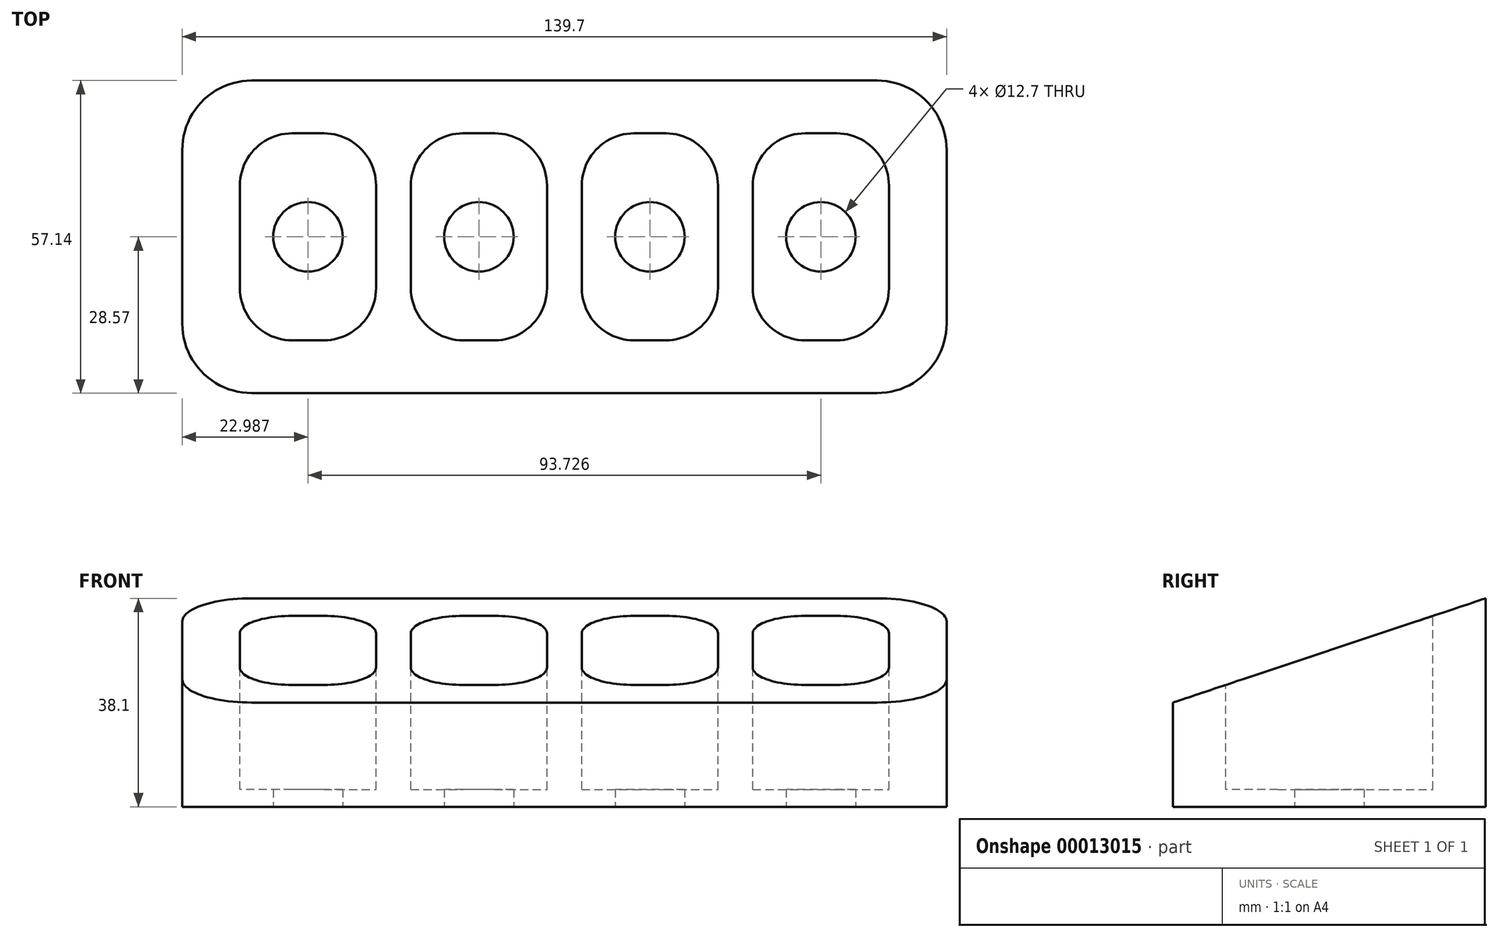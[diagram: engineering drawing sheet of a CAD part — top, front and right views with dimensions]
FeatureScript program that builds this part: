
annotation { "Feature Type Name" : "Feature", "Feature Type Description" : "" }
export const myFeature = defineFeature(function(context is Context, id is Id, definition is map)
    precondition{}
    {
        {
            var Q0;
            Q0=qCreatedBy(makeId("Top.planeOp"),FACE);
            var sketch = newSketch(context, id + "F0", { "sketchPlane" : qUnion([Q0])});
            skLineSegment(sketch, "E0.rect.bottom", {"start": v(69.85, 28.58) * mm, "end": v(-69.85, 28.58) * mm});
            skLineSegment(sketch, "E0.rect.top", {"start": v(69.85, -28.57) * mm, "end": v(-69.85, -28.57) * mm});
            skLineSegment(sketch, "E0.rect.left", {"start": v(69.85, 28.58) * mm, "end": v(69.85, -28.57) * mm});
            skLineSegment(sketch, "E0.rect.right", {"start": v(-69.85, 28.58) * mm, "end": v(-69.85, -28.57) * mm});
            skPoint(sketch, "E0.rect.middle", {"position": v(0, 0) * mm});
            skSolve(sketch);
        }
        {
            var Q0;
            Q0 = qSketchRegion(id + "F0", true);
            extrude(context, id + "F1", {"entities" : qUnion([Q0]), "depth" : 38.1 * mm});
        }
        {
            var Q0;
            Q0=makeQuery(id+"F1.opExtrude","CAP_FACE",FACE,{"disambiguationData":[OSD([sQuery(id+"F0.wireOp",EDGE,"E0.rect.bottom"),sQuery(id+"F0.wireOp",EDGE,"E0.rect.top"),sQuery(id+"F0.wireOp",EDGE,"E0.rect.left"),sQuery(id+"F0.wireOp",EDGE,"E0.rect.right")])],"isStart":false});
            var sketch = newSketch(context, id + "F2", { "sketchPlane" : qUnion([Q0])});
            skLineSegment(sketch, "E1.rect.bottom", {"start": v(-3.18, -18.92) * mm, "end": v(-28.07, -18.92) * mm});
            skLineSegment(sketch, "E1.rect.top", {"start": v(-3.17, 18.92) * mm, "end": v(-28.07, 18.92) * mm});
            skLineSegment(sketch, "E1.rect.left", {"start": v(-3.18, -18.92) * mm, "end": v(-3.17, 18.92) * mm});
            skLineSegment(sketch, "E1.rect.right", {"start": v(-28.07, -18.92) * mm, "end": v(-28.07, 18.92) * mm});
            skPoint(sketch, "E1.rect.middle", {"position": v(-15.62, 0) * mm});
            skLineSegment(sketch, "E2", {"start": v(0, -48.44) * mm, "end": v(0, 55.61) * mm, "construction": true});
            skLineSegment(sketch, "E3.1.0.0", {"start": v(-34.42, 18.92) * mm, "end": v(-59.3, 18.92) * mm});
            skLineSegment(sketch, "E3.1.0.1", {"start": v(-59.3, -18.92) * mm, "end": v(-59.3, 18.92) * mm});
            skLineSegment(sketch, "E3.1.0.2", {"start": v(-34.42, -18.92) * mm, "end": v(-34.42, 18.92) * mm});
            skLineSegment(sketch, "E3.1.0.3", {"start": v(-34.42, -18.92) * mm, "end": v(-59.3, -18.92) * mm});
            skLineSegment(sketch, "E3.direction1", {"start": v(-28.07, 18.92) * mm, "end": v(-59.3, 18.92) * mm});
            skLineSegment(sketch, "E4.0.MirrorCS", {"start": v(3.18, -18.92) * mm, "end": v(3.17, 18.92) * mm});
            skLineSegment(sketch, "E4.1.MirrorCS", {"start": v(3.17, 18.92) * mm, "end": v(28.07, 18.92) * mm});
            skLineSegment(sketch, "E4.2.MirrorCS", {"start": v(28.07, -18.92) * mm, "end": v(28.07, 18.92) * mm});
            skLineSegment(sketch, "E4.3.MirrorCS", {"start": v(3.18, -18.92) * mm, "end": v(28.07, -18.92) * mm});
            skLineSegment(sketch, "E4.4.MirrorCS", {"start": v(34.42, -18.92) * mm, "end": v(59.3, -18.92) * mm});
            skLineSegment(sketch, "E4.5.MirrorCS", {"start": v(59.3, -18.92) * mm, "end": v(59.3, 18.92) * mm});
            skLineSegment(sketch, "E4.6.MirrorCS", {"start": v(34.42, 18.92) * mm, "end": v(59.3, 18.92) * mm});
            skLineSegment(sketch, "E4.7.MirrorCS", {"start": v(34.42, -18.92) * mm, "end": v(34.42, 18.92) * mm});
            skSolve(sketch);
        }
        {
            var Q0;
            Q0 = qSketchRegion(id + "F2", true);
            extrude(context, id + "F3", {"entities" : qUnion([Q0]), "operationType" : NewBodyOperationType.REMOVE, "oppositeDirection" : true, "depth" : 34.92 * mm});
        }
        {
            var Q0;
            Q0=makeQuery(id+"F1.opExtrude","SWEPT_FACE",FACE,{"disambiguationData":[OSD([sQuery(id+"F0.wireOp",EDGE,"E0.rect.left")])]});
            var sketch = newSketch(context, id + "F4", { "sketchPlane" : qUnion([Q0])});
            skLineSegment(sketch, "E5", {"start": v(28.57, 38.1) * mm, "end": v(-28.58, 19.05) * mm});
            skLineSegment(sketch, "E6", {"start": v(-28.58, 19.05) * mm, "end": v(-28.58, 38.1) * mm});
            skLineSegment(sketch, "E7", {"start": v(-28.58, 38.1) * mm, "end": v(28.57, 38.1) * mm});
            skSolve(sketch);
        }
        {
            var Q0;
            Q0=makeQuery(id+"F4.imprint","IMPRINT",FACE,{"disambiguationData":[TD([[makeQuery(id+"F4.imprint","IMPRINT",EDGE,{"derivedFrom":sQuery(id+"F4.wireOp",EDGE,"E5")}),-1.0]])]});
            extrude(context, id + "F5", {"entities" : qUnion([Q0]), "operationType" : NewBodyOperationType.REMOVE, "endBound" : BoundingType.THROUGH_ALL, "oppositeDirection" : true, "depth" : 25.4 * mm});
        }
        {
            var Q0;
            Q0=makeQuery(id+"F1.opExtrude","SWEPT_EDGE",EDGE,{"disambiguationData":[OSD([sQuery(id+"F0.wireOp",EDGE,"E0.rect.top"),sQuery(id+"F0.wireOp",EDGE,"E0.rect.left")])]});
            var Q1;
            Q1=makeQuery(id+"F1.opExtrude","SWEPT_EDGE",EDGE,{"disambiguationData":[OSD([sQuery(id+"F0.wireOp",EDGE,"E0.rect.bottom"),sQuery(id+"F0.wireOp",EDGE,"E0.rect.left")])]});
            var Q2;
            Q2=makeQuery(id+"F1.opExtrude","SWEPT_EDGE",EDGE,{"disambiguationData":[OSD([sQuery(id+"F0.wireOp",EDGE,"E0.rect.top"),sQuery(id+"F0.wireOp",EDGE,"E0.rect.right")])]});
            var Q3;
            Q3=makeQuery(id+"F1.opExtrude","SWEPT_EDGE",EDGE,{"disambiguationData":[OSD([sQuery(id+"F0.wireOp",EDGE,"E0.rect.bottom"),sQuery(id+"F0.wireOp",EDGE,"E0.rect.right")])]});
            fillet(context, id + "F6", {"entities" : qUnion([Q0, Q1, Q2, Q3]), "radius" : 12.7 * mm, "tangentPropagation" : true, "allowEdgeOverflow" : false});
        }
        {
            var Q0;
            Q0=makeQuery(id+"F3.boolean.opBoolean","COPY",EDGE,{"derivedFrom":makeQuery(id+"F3.opExtrude","SWEPT_EDGE",EDGE,{"disambiguationData":[OSD([sQuery(id+"F2.wireOp",EDGE,"E3.1.0.1"),sQuery(id+"F2.wireOp",EDGE,"E3.direction1")])]})});
            var Q1;
            Q1=makeQuery(id+"F3.boolean.opBoolean","COPY",EDGE,{"derivedFrom":makeQuery(id+"F3.opExtrude","SWEPT_EDGE",EDGE,{"disambiguationData":[OSD([sQuery(id+"F2.wireOp",EDGE,"E3.1.0.2"),sQuery(id+"F2.wireOp",EDGE,"E3.direction1")])]})});
            var Q2;
            Q2=makeQuery(id+"F3.boolean.opBoolean","COPY",EDGE,{"derivedFrom":makeQuery(id+"F3.opExtrude","SWEPT_EDGE",EDGE,{"disambiguationData":[OSD([sQuery(id+"F2.wireOp",EDGE,"E1.rect.top"),sQuery(id+"F2.wireOp",EDGE,"E1.rect.right")])]})});
            var Q3;
            Q3=makeQuery(id+"F3.boolean.opBoolean","COPY",EDGE,{"derivedFrom":makeQuery(id+"F3.opExtrude","SWEPT_EDGE",EDGE,{"disambiguationData":[OSD([sQuery(id+"F2.wireOp",EDGE,"E1.rect.top"),sQuery(id+"F2.wireOp",EDGE,"E1.rect.left")])]})});
            var Q4;
            Q4=makeQuery(id+"F3.boolean.opBoolean","COPY",EDGE,{"derivedFrom":makeQuery(id+"F3.opExtrude","SWEPT_EDGE",EDGE,{"disambiguationData":[OSD([sQuery(id+"F2.wireOp",EDGE,"E4.1.MirrorCS"),sQuery(id+"F2.wireOp",EDGE,"E4.2.MirrorCS")])]})});
            var Q5;
            Q5=makeQuery(id+"F3.boolean.opBoolean","COPY",EDGE,{"derivedFrom":makeQuery(id+"F3.opExtrude","SWEPT_EDGE",EDGE,{"disambiguationData":[OSD([sQuery(id+"F2.wireOp",EDGE,"E4.5.MirrorCS"),sQuery(id+"F2.wireOp",EDGE,"E4.6.MirrorCS")])]})});
            var Q6;
            Q6=makeQuery(id+"F3.boolean.opBoolean","COPY",EDGE,{"derivedFrom":makeQuery(id+"F3.opExtrude","SWEPT_EDGE",EDGE,{"disambiguationData":[OSD([sQuery(id+"F2.wireOp",EDGE,"E4.6.MirrorCS"),sQuery(id+"F2.wireOp",EDGE,"E4.7.MirrorCS")])]})});
            var Q7;
            Q7=makeQuery(id+"F3.boolean.opBoolean","COPY",EDGE,{"derivedFrom":makeQuery(id+"F3.opExtrude","SWEPT_EDGE",EDGE,{"disambiguationData":[OSD([sQuery(id+"F2.wireOp",EDGE,"E4.0.MirrorCS"),sQuery(id+"F2.wireOp",EDGE,"E4.1.MirrorCS")])]})});
            var Q8;
            Q8=makeQuery(id+"F3.boolean.opBoolean","COPY",EDGE,{"derivedFrom":makeQuery(id+"F3.opExtrude","SWEPT_EDGE",EDGE,{"disambiguationData":[OSD([sQuery(id+"F2.wireOp",EDGE,"E4.2.MirrorCS"),sQuery(id+"F2.wireOp",EDGE,"E4.3.MirrorCS")])]})});
            var Q9;
            Q9=makeQuery(id+"F3.boolean.opBoolean","COPY",EDGE,{"derivedFrom":makeQuery(id+"F3.opExtrude","SWEPT_EDGE",EDGE,{"disambiguationData":[OSD([sQuery(id+"F2.wireOp",EDGE,"E4.4.MirrorCS"),sQuery(id+"F2.wireOp",EDGE,"E4.5.MirrorCS")])]})});
            var Q10;
            Q10=makeQuery(id+"F3.boolean.opBoolean","COPY",EDGE,{"derivedFrom":makeQuery(id+"F3.opExtrude","SWEPT_EDGE",EDGE,{"disambiguationData":[OSD([sQuery(id+"F2.wireOp",EDGE,"E1.rect.bottom"),sQuery(id+"F2.wireOp",EDGE,"E1.rect.left")])]})});
            var Q11;
            Q11=makeQuery(id+"F3.boolean.opBoolean","COPY",EDGE,{"derivedFrom":makeQuery(id+"F3.opExtrude","SWEPT_EDGE",EDGE,{"disambiguationData":[OSD([sQuery(id+"F2.wireOp",EDGE,"E3.1.0.2"),sQuery(id+"F2.wireOp",EDGE,"E3.1.0.3")])]})});
            var Q12;
            Q12=makeQuery(id+"F3.boolean.opBoolean","COPY",EDGE,{"derivedFrom":makeQuery(id+"F3.opExtrude","SWEPT_EDGE",EDGE,{"disambiguationData":[OSD([sQuery(id+"F2.wireOp",EDGE,"E3.1.0.1"),sQuery(id+"F2.wireOp",EDGE,"E3.1.0.3")])]})});
            var Q13;
            Q13=makeQuery(id+"F3.boolean.opBoolean","COPY",EDGE,{"derivedFrom":makeQuery(id+"F3.opExtrude","SWEPT_EDGE",EDGE,{"disambiguationData":[OSD([sQuery(id+"F2.wireOp",EDGE,"E1.rect.bottom"),sQuery(id+"F2.wireOp",EDGE,"E1.rect.right")])]})});
            var Q14;
            Q14=makeQuery(id+"F3.boolean.opBoolean","COPY",EDGE,{"derivedFrom":makeQuery(id+"F3.opExtrude","SWEPT_EDGE",EDGE,{"disambiguationData":[OSD([sQuery(id+"F2.wireOp",EDGE,"E4.0.MirrorCS"),sQuery(id+"F2.wireOp",EDGE,"E4.3.MirrorCS")])]})});
            var Q15;
            Q15=makeQuery(id+"F3.boolean.opBoolean","COPY",EDGE,{"derivedFrom":makeQuery(id+"F3.opExtrude","SWEPT_EDGE",EDGE,{"disambiguationData":[OSD([sQuery(id+"F2.wireOp",EDGE,"E4.4.MirrorCS"),sQuery(id+"F2.wireOp",EDGE,"E4.7.MirrorCS")])]})});
            fillet(context, id + "F7", {"entities" : qUnion([Q0, Q1, Q2, Q3, Q4, Q5, Q6, Q7, Q8, Q9, Q10, Q11, Q12, Q13, Q14, Q15]), "radius" : 9.52 * mm, "tangentPropagation" : true, "allowEdgeOverflow" : false});
        }
        {
            var Q0;
            Q0=qCreatedBy(makeId("Top.planeOp"),FACE);
            var sketch = newSketch(context, id + "F8", { "sketchPlane" : qUnion([Q0])});
            skLineSegment(sketch, "E8", {"start": v(-46.86, 18.92) * mm, "end": v(-46.86, -18.92) * mm, "construction": true});
            skCircle(sketch, "E9", {"center": v(-46.86, 0) * mm, "radius": 6.35 * mm});
            skCircle(sketch, "E10.1.0.0", {"center": v(-15.62, 0) * mm, "radius": 6.35 * mm});
            skCircle(sketch, "E10.2.0.0", {"center": v(15.62, 0) * mm, "radius": 6.35 * mm});
            skCircle(sketch, "E10.3.0.0", {"center": v(46.86, 0) * mm, "radius": 6.35 * mm});
            skLineSegment(sketch, "E10.direction1", {"start": v(-46.86, 0) * mm, "end": v(-15.62, 0) * mm, "construction": true});
            skSolve(sketch);
        }
        {
            var Q0;
            Q0 = qSketchRegion(id + "F8", true);
            extrude(context, id + "F9", {"entities" : qUnion([Q0]), "operationType" : NewBodyOperationType.REMOVE, "endBound" : BoundingType.THROUGH_ALL, "depth" : 25.4 * mm});
        }
    });
